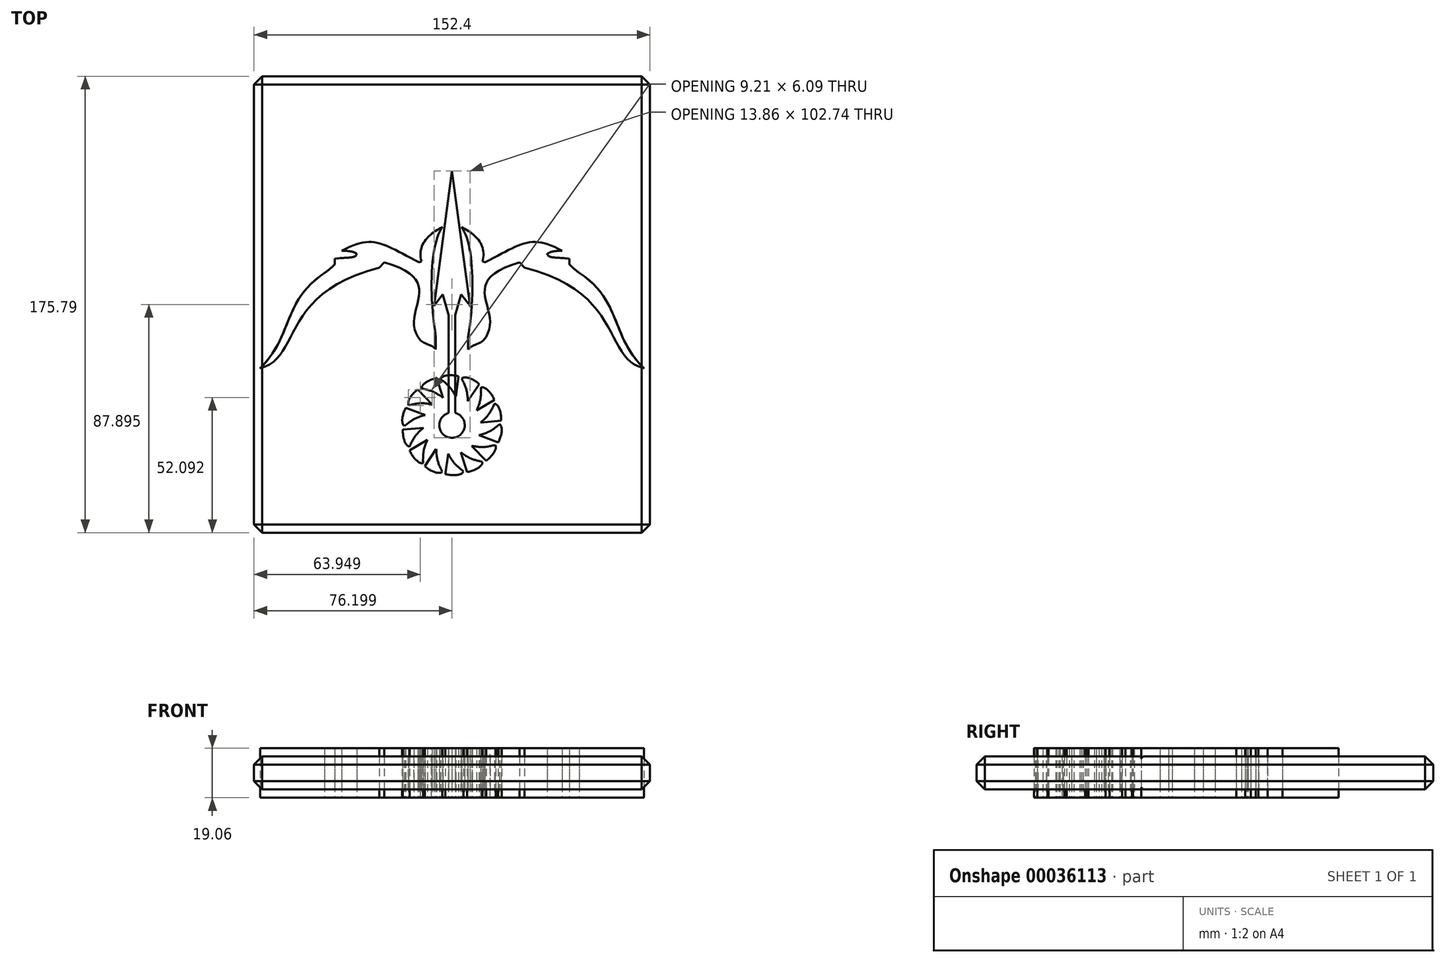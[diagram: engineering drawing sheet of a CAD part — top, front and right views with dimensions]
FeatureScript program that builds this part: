
annotation { "Feature Type Name" : "Feature", "Feature Type Description" : "" }
export const myFeature = defineFeature(function(context is Context, id is Id, definition is map)
    precondition{}
    {
        {
            var Q0;
            Q0=qCreatedBy(makeId("Top.planeOp"),FACE);
            var sketch = newSketch(context, id + "F0", { "sketchPlane" : qUnion([Q0])});
            skCircle(sketch, "E0", {"center": v(-0.8, 30.82) * mm, "radius": 4.9 * mm});
            skLineSegment(sketch, "E1", {"start": v(0.47, 35.55) * mm, "end": v(0.47, 73.19) * mm});
            skLineSegment(sketch, "E2", {"start": v(-2.07, 35.55) * mm, "end": v(-2.07, 73.19) * mm});
            skLineSegment(sketch, "E3", {"start": v(-2.07, 73.19) * mm, "end": v(0.47, 73.19) * mm});
            skPoint(sketch, "E4.endSnap0", {"position": v(-0.8, 73.19) * mm});
            skLineSegment(sketch, "E5", {"start": v(-2.07, 73.19) * mm, "end": v(-4.36, 81.25) * mm});
            skLineSegment(sketch, "E6", {"start": v(-4.36, 81.25) * mm, "end": v(-7.73, 76.73) * mm});
            skLineSegment(sketch, "E7", {"start": v(-7.73, 76.73) * mm, "end": v(-0.8, 128.68) * mm});
            skFitSpline(sketch, "E8", {"points": [v(-4.42, 107.15) * mm, v(-7, 64.79) * mm], "startDerivative": vector(-13.3, -17.18) * mm, "endDerivative": vector(9.05, -55.79) * mm});
            skLineSegment(sketch, "E9", {"start": v(-7, 64.79) * mm, "end": v(-7, 59.98) * mm});
            skFitSpline(sketch, "E10", {"points": [v(-7, 59.98) * mm, v(-12.86, 63.37) * mm], "startDerivative": vector(-4.37, 5.72) * mm, "endDerivative": vector(-8.5, 5.91) * mm});
            skFitSpline(sketch, "E11", {"points": [v(-26.83, 93.47) * mm, v(-12.86, 63.37) * mm], "startDerivative": vector(78.07, -22.52) * mm, "endDerivative": vector(28.31, -34.05) * mm});
            skLineSegment(sketch, "E12", {"start": v(-26.83, 93.47) * mm, "end": v(-28.76, 91.45) * mm});
            skFitSpline(sketch, "E13", {"points": [v(-74.63, 52.78) * mm, v(-28.76, 91.45) * mm], "startDerivative": vector(47.27, 10.33) * mm, "endDerivative": vector(115.7, 29.12) * mm});
            skFitSpline(sketch, "E14", {"points": [v(-74.63, 52.78) * mm, v(-49.82, 89.4) * mm], "startDerivative": vector(38.39, 37.5) * mm, "endDerivative": vector(48.6, 31.61) * mm});
            skFitSpline(sketch, "E15", {"points": [v(-49.82, 89.4) * mm, v(-45.92, 92.82) * mm], "startDerivative": vector(4.18, 3.26) * mm, "endDerivative": vector(2.79, 3.31) * mm});
            skLineSegment(sketch, "E16", {"start": v(-45.92, 92.82) * mm, "end": v(-45.92, 94.91) * mm});
            skFitSpline(sketch, "E17", {"points": [v(-45.92, 94.91) * mm, v(-37.44, 96.89) * mm], "startDerivative": vector(17.2, 1.97) * mm, "endDerivative": vector(1.06, 5.55) * mm});
            skFitSpline(sketch, "E18", {"points": [v(-43.25, 97.9) * mm, v(-37.44, 96.89) * mm], "startDerivative": vector(6.75, 0.47) * mm, "endDerivative": vector(4.51, -2.6) * mm});
            skFitSpline(sketch, "E19", {"points": [v(-43.25, 97.9) * mm, v(-13.44, 93.56) * mm], "startDerivative": vector(36.4, 20.62) * mm, "endDerivative": vector(41.88, -20.75) * mm});
            skLineSegment(sketch, "E20", {"start": v(-13.44, 93.56) * mm, "end": v(-12.53, 93.88) * mm});
            skFitSpline(sketch, "E21", {"points": [v(-12.53, 93.88) * mm, v(-4.42, 107.15) * mm], "startDerivative": vector(-5.39, 18.96) * mm, "endDerivative": vector(16.46, 8.3) * mm});
            skLineSegment(sketch, "E22.MirrorCS", {"start": v(6.13, 76.73) * mm, "end": v(-0.8, 128.68) * mm});
            skLineSegment(sketch, "E23.MirrorCS", {"start": v(0.47, 73.19) * mm, "end": v(2.76, 81.25) * mm});
            skLineSegment(sketch, "E24.MirrorCS", {"start": v(2.76, 81.25) * mm, "end": v(6.13, 76.73) * mm});
            skFitSpline(sketch, "E25.MirrorCS", {"points": [v(2.82, 107.15) * mm, v(5.4, 64.79) * mm], "startDerivative": vector(13.3, -17.18) * mm, "endDerivative": vector(-9.05, -55.79) * mm});
            skLineSegment(sketch, "E26.MirrorCS", {"start": v(5.4, 64.79) * mm, "end": v(5.4, 59.98) * mm});
            skFitSpline(sketch, "E27.MirrorCS", {"points": [v(5.4, 59.98) * mm, v(11.26, 63.37) * mm], "startDerivative": vector(4.37, 5.72) * mm, "endDerivative": vector(8.5, 5.91) * mm});
            skFitSpline(sketch, "E28.MirrorCS", {"points": [v(25.22, 93.47) * mm, v(11.26, 63.37) * mm], "startDerivative": vector(-78.07, -22.52) * mm, "endDerivative": vector(-28.31, -34.05) * mm});
            skLineSegment(sketch, "E29.MirrorCS", {"start": v(25.22, 93.47) * mm, "end": v(27.15, 91.45) * mm});
            skFitSpline(sketch, "E30.MirrorCS", {"points": [v(73.03, 52.78) * mm, v(27.15, 91.45) * mm], "startDerivative": vector(-47.27, 10.33) * mm, "endDerivative": vector(-115.7, 29.12) * mm});
            skFitSpline(sketch, "E31.MirrorCS", {"points": [v(73.03, 52.78) * mm, v(48.21, 89.4) * mm], "startDerivative": vector(-38.39, 37.5) * mm, "endDerivative": vector(-48.6, 31.61) * mm});
            skFitSpline(sketch, "E32.MirrorCS", {"points": [v(48.21, 89.4) * mm, v(44.32, 92.82) * mm], "startDerivative": vector(-4.18, 3.26) * mm, "endDerivative": vector(-2.79, 3.31) * mm});
            skLineSegment(sketch, "E33.MirrorCS", {"start": v(44.32, 92.82) * mm, "end": v(44.32, 94.91) * mm});
            skFitSpline(sketch, "E34.MirrorCS", {"points": [v(44.32, 94.91) * mm, v(35.83, 96.89) * mm], "startDerivative": vector(-17.2, 1.97) * mm, "endDerivative": vector(-1.06, 5.55) * mm});
            skFitSpline(sketch, "E35.MirrorCS", {"points": [v(41.65, 97.9) * mm, v(35.83, 96.89) * mm], "startDerivative": vector(-6.75, 0.47) * mm, "endDerivative": vector(-4.51, -2.6) * mm});
            skFitSpline(sketch, "E36.MirrorCS", {"points": [v(41.65, 97.9) * mm, v(11.83, 93.56) * mm], "startDerivative": vector(-36.4, 20.62) * mm, "endDerivative": vector(-41.88, -20.75) * mm});
            skLineSegment(sketch, "E37.MirrorCS", {"start": v(11.83, 93.56) * mm, "end": v(10.93, 93.88) * mm});
            skFitSpline(sketch, "E38.MirrorCS", {"points": [v(10.93, 93.88) * mm, v(2.82, 107.15) * mm], "startDerivative": vector(5.39, 18.96) * mm, "endDerivative": vector(-16.46, 8.3) * mm});
            skLineSegment(sketch, "E39", {"start": v(-8.45, 38.81) * mm, "end": v(-13.92, 44.55) * mm});
            skFitSpline(sketch, "E40", {"points": [v(-8.45, 38.81) * mm, v(-17.45, 38.45) * mm], "startDerivative": vector(-12.12, 2.2) * mm, "endDerivative": vector(-10.67, -2.62) * mm});
            skFitSpline(sketch, "E41", {"points": [v(-13.92, 44.55) * mm, v(-17.45, 38.45) * mm], "startDerivative": vector(-7.13, -5.18) * mm, "endDerivative": vector(2.72, -4.59) * mm});
            skLineSegment(sketch, "E42", {"start": v(-2.07, 35.55) * mm, "end": v(0.47, 35.55) * mm});
            skLineSegment(sketch, "E43", {"start": v(-0.8, -10.6) * mm, "end": v(75.4, -10.6) * mm});
            skLineSegment(sketch, "E44", {"start": v(75.4, -10.6) * mm, "end": v(75.4, 77.3) * mm});
            skLineSegment(sketch, "E45", {"start": v(75.4, 77.3) * mm, "end": v(75.4, 165.2) * mm});
            skLineSegment(sketch, "E46", {"start": v(75.4, 165.2) * mm, "end": v(-77, 165.2) * mm});
            skLineSegment(sketch, "E47", {"start": v(-77, 165.2) * mm, "end": v(-77, -10.6) * mm});
            skLineSegment(sketch, "E48", {"start": v(-77, -10.6) * mm, "end": v(-0.8, -10.6) * mm});
            skSolve(sketch);
        }
        {
            var Q0;
            Q0=makeQuery(id+"F0.imprint","IMPRINT",FACE,{"disambiguationData":[TD([[makeQuery(id+"F0.imprint","IMPRINT",EDGE,{"derivedFrom":sQuery(id+"F0.wireOp",EDGE,"E25.MirrorCS")}),1.0]])]});
            var Q1;
            Q1=makeQuery(id+"F0.imprint","IMPRINT",FACE,{"disambiguationData":[TD([[makeQuery(id+"F0.imprint","IMPRINT",EDGE,{"derivedFrom":sQuery(id+"F0.wireOp",EDGE,"E3")}),1.0]])]});
            var Q2;
            Q2=makeQuery(id+"F0.imprint","IMPRINT",FACE,{"disambiguationData":[TD([[makeQuery(id+"F0.imprint","IMPRINT",EDGE,{"derivedFrom":sQuery(id+"F0.wireOp",EDGE,"E8")}),-1.0]])]});
            var Q3;
            {var subQ1=sQuery(id+"F0.wireOp",EDGE,"E1");Q3=makeQuery(id+"F0.imprint","IMPRINT",FACE,{"disambiguationData":[TD([[makeQuery(id+"F0.imprint","IMPRINT",EDGE,{"derivedFrom":subQ1}),1.0]])]});}
            var Q4;
            {var subQ0=sQuery(id+"F0.wireOp",EDGE,"E42");Q4=makeQuery(id+"F0.imprint","IMPRINT",FACE,{"disambiguationData":[TD([[makeQuery(id+"F0.imprint","IMPRINT",EDGE,{"derivedFrom":subQ0}),-1.0]])]});}
            var Q5;
            Q5=makeQuery(id+"F0.imprint","IMPRINT",FACE,{"disambiguationData":[TD([[makeQuery(id+"F0.imprint","IMPRINT",EDGE,{"derivedFrom":sQuery(id+"F0.wireOp",EDGE,"E39")}),1.0]])]});
            var Q6;
            {var subQ0=sQuery(id+"F0.wireOp",EDGE,"E42");Q6=makeQuery(id+"F0.imprint","IMPRINT",FACE,{"disambiguationData":[TD([[makeQuery(id+"F0.imprint","IMPRINT",EDGE,{"derivedFrom":subQ0}),1.0]])]});}
            extrude(context, id + "F1", {"entities" : qUnion([Q0, Q1, Q2, Q3, Q4, Q5, Q6]), "endBound" : BoundingType.SYMMETRIC, "depth" : 19.05 * mm});
        }
        {
            var Q0;
            Q0=qCreatedBy(makeId("Front.planeOp"),FACE);
            cPlane(context, id + "F2", {"entities" : qUnion([Q0]), "cplaneType" : CPlaneType.OFFSET, "offset" : 30.82 * mm, "oppositeDirection" : true, "width" : 152.4 * mm, "height" : 152.4 * mm});
        }
        {
            var Q0;
            Q0=qCreatedBy(id+"F2.planeOp",FACE);
            var sketch = newSketch(context, id + "F3", { "sketchPlane" : qUnion([Q0])});
            skPoint(sketch, "E49.0", {"position": v(-0.8, 0) * mm});
            skLineSegment(sketch, "E50", {"start": v(-0.8, 0) * mm, "end": v(-0.8, 51.5) * mm});
            skSolve(sketch);
        }
        {
            var Q0;
            Q0=makeQuery(id+"F1.opExtrude","SWEPT_BODY",BODY,{"disambiguationData":[OSD([sQuery(id+"F0.wireOp",EDGE,"E39"),sQuery(id+"F0.wireOp",EDGE,"E40"),sQuery(id+"F0.wireOp",EDGE,"E41")])]});
            var Q1;
            Q1=sQuery(id+"F3.wireOp",EDGE,"E50");
            circularPattern(context, id + "F4", {"entities" : qUnion([Q0]), "axis" : qUnion([Q1]), "angle" : 25.71 * degree, "instanceCount" : 14});
        }
        {
            var Q0;
            {var subQ3=sQuery(id+"F0.wireOp",EDGE,"E1");Q0=makeQuery(id+"F0.imprint","IMPRINT",FACE,{"disambiguationData":[TD([[makeQuery(id+"F0.imprint","IMPRINT",EDGE,{"derivedFrom":subQ3}),-1.0]])]});}
            extrude(context, id + "F5", {"entities" : qUnion([Q0]), "endBound" : BoundingType.SYMMETRIC, "depth" : 12.7 * mm});
        }
        {
            var Q0;
            Q0=makeQuery(id+"F5.opExtrude","CAP_EDGE",EDGE,{"disambiguationData":[OSD([sQuery(id+"F0.wireOp",EDGE,"E46")])],"isStart":false});
            var Q1;
            Q1=makeQuery(id+"F5.opExtrude","CAP_EDGE",EDGE,{"disambiguationData":[OSD([sQuery(id+"F0.wireOp",EDGE,"E46")])],"isStart":true});
            var Q2;
            Q2=makeQuery(id+"F5.opExtrude","CAP_EDGE",EDGE,{"disambiguationData":[OSD([sQuery(id+"F0.wireOp",EDGE,"E44"),sQuery(id+"F0.wireOp",EDGE,"E45")])],"isStart":false});
            var Q3;
            Q3=makeQuery(id+"F5.opExtrude","CAP_EDGE",EDGE,{"disambiguationData":[OSD([sQuery(id+"F0.wireOp",EDGE,"E44"),sQuery(id+"F0.wireOp",EDGE,"E45")])],"isStart":true});
            var Q4;
            Q4=makeQuery(id+"F5.opExtrude","CAP_EDGE",EDGE,{"disambiguationData":[OSD([sQuery(id+"F0.wireOp",EDGE,"E47")])],"isStart":true});
            var Q5;
            Q5=makeQuery(id+"F5.opExtrude","CAP_EDGE",EDGE,{"disambiguationData":[OSD([sQuery(id+"F0.wireOp",EDGE,"E47")])],"isStart":false});
            var Q6;
            Q6=makeQuery(id+"F5.opExtrude","CAP_EDGE",EDGE,{"disambiguationData":[OSD([sQuery(id+"F0.wireOp",EDGE,"E43"),sQuery(id+"F0.wireOp",EDGE,"E48")])],"isStart":false});
            var Q7;
            Q7=makeQuery(id+"F5.opExtrude","CAP_EDGE",EDGE,{"disambiguationData":[OSD([sQuery(id+"F0.wireOp",EDGE,"E43"),sQuery(id+"F0.wireOp",EDGE,"E48")])],"isStart":true});
            var Q8;
            Q8=makeQuery(id+"F5.opExtrude","SWEPT_EDGE",EDGE,{"disambiguationData":[OSD([sQuery(id+"F0.wireOp",EDGE,"E46"),sQuery(id+"F0.wireOp",EDGE,"E47")])]});
            var Q9;
            Q9=makeQuery(id+"F5.opExtrude","SWEPT_EDGE",EDGE,{"disambiguationData":[OSD([sQuery(id+"F0.wireOp",EDGE,"E45"),sQuery(id+"F0.wireOp",EDGE,"E46")])]});
            var Q10;
            Q10=makeQuery(id+"F5.opExtrude","SWEPT_EDGE",EDGE,{"disambiguationData":[OSD([sQuery(id+"F0.wireOp",EDGE,"E43"),sQuery(id+"F0.wireOp",EDGE,"E44")])]});
            var Q11;
            Q11=makeQuery(id+"F5.opExtrude","SWEPT_EDGE",EDGE,{"disambiguationData":[OSD([sQuery(id+"F0.wireOp",EDGE,"E47"),sQuery(id+"F0.wireOp",EDGE,"E48")])]});
            chamfer(context, id + "F6", {"entities" : qUnion([Q0, Q1, Q2, Q3, Q4, Q5, Q6, Q7, Q8, Q9, Q10, Q11]), "width" : 3.17 * mm, "tangentPropagation" : true});
        }
    });
